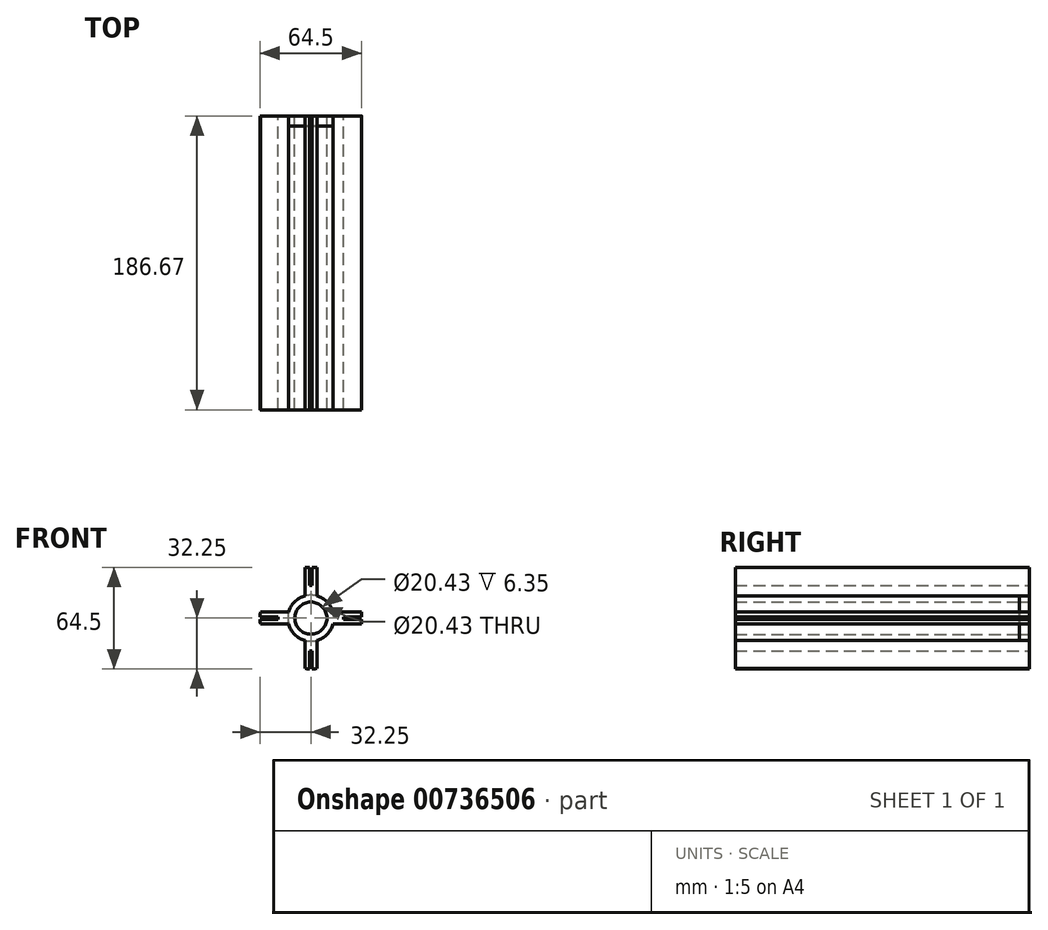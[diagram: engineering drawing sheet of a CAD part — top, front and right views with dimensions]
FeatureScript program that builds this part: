
annotation { "Feature Type Name" : "Feature", "Feature Type Description" : "" }
export const myFeature = defineFeature(function(context is Context, id is Id, definition is map)
    precondition{}
    {
        {
            var Q0;
            Q0=qCreatedBy(makeId("Front.planeOp"),FACE);
            var sketch = newSketch(context, id + "F0", { "sketchPlane" : qUnion([Q0])});
            skCircle(sketch, "E0", {"center": v(0, 0) * mm, "radius": 32.26 * mm});
            skCircle(sketch, "E1", {"center": v(-18.27, 15.72) * mm, "radius": 1.59 * mm});
            skCircle(sketch, "E2.MirrorC", {"center": v(18.27, 15.72) * mm, "radius": 1.59 * mm});
            skCircle(sketch, "E3.MirrorC", {"center": v(18.27, -15.72) * mm, "radius": 1.59 * mm});
            skCircle(sketch, "E4.MirrorC", {"center": v(-18.27, -15.72) * mm, "radius": 1.59 * mm});
            skCircle(sketch, "E5", {"center": v(0, 0) * mm, "radius": 14.6 * mm});
            skLineSegment(sketch, "E6", {"start": v(-20.83, 0) * mm, "end": v(-20.83, 0.83) * mm});
            skLineSegment(sketch, "E7", {"start": v(-20.83, 0.83) * mm, "end": v(-32.25, 0.83) * mm});
            skLineSegment(sketch, "E8.MirrorCS", {"start": v(-20.83, -0.83) * mm, "end": v(-32.25, -0.83) * mm});
            skLineSegment(sketch, "E9.MirrorCS", {"start": v(-20.83, 0) * mm, "end": v(-20.83, -0.83) * mm});
            skLineSegment(sketch, "E10.MirrorCS", {"start": v(20.83, 0.83) * mm, "end": v(32.25, 0.83) * mm});
            skLineSegment(sketch, "E11.MirrorCS", {"start": v(20.83, 0) * mm, "end": v(20.83, 0.83) * mm});
            skLineSegment(sketch, "E12.MirrorCS", {"start": v(20.83, -0.83) * mm, "end": v(32.25, -0.83) * mm});
            skLineSegment(sketch, "E13.MirrorCS", {"start": v(20.83, 0) * mm, "end": v(20.83, -0.83) * mm});
            skLineSegment(sketch, "E14", {"start": v(0, -20.83) * mm, "end": v(0.83, -20.83) * mm});
            skLineSegment(sketch, "E15", {"start": v(0.83, -20.83) * mm, "end": v(0.83, -32.25) * mm});
            skLineSegment(sketch, "E16.MirrorCS", {"start": v(0, -20.83) * mm, "end": v(-0.83, -20.83) * mm});
            skLineSegment(sketch, "E17.MirrorCS", {"start": v(-0.83, -20.83) * mm, "end": v(-0.83, -32.25) * mm});
            skLineSegment(sketch, "E18.MirrorCS", {"start": v(0.83, 20.83) * mm, "end": v(0.83, 32.25) * mm});
            skLineSegment(sketch, "E19.MirrorCS", {"start": v(-0.83, 20.83) * mm, "end": v(-0.83, 32.25) * mm});
            skLineSegment(sketch, "E20.MirrorCS", {"start": v(0, 20.83) * mm, "end": v(-0.83, 20.83) * mm});
            skLineSegment(sketch, "E21.MirrorCS", {"start": v(0, 20.83) * mm, "end": v(0.83, 20.83) * mm});
            skCircle(sketch, "E22", {"center": v(0, 0) * mm, "radius": 10.21 * mm});
            skLineSegment(sketch, "E23", {"start": v(0.83, 20.83) * mm, "end": v(3.83, 20.83) * mm});
            skLineSegment(sketch, "E24", {"start": v(3.83, 20.83) * mm, "end": v(3.83, 32.03) * mm});
            skLineSegment(sketch, "E25.MirrorCS", {"start": v(-3.83, 20.83) * mm, "end": v(-3.83, 32.03) * mm});
            skLineSegment(sketch, "E26.MirrorCS", {"start": v(-0.83, 20.83) * mm, "end": v(-3.83, 20.83) * mm});
            skLineSegment(sketch, "E27.MirrorCS", {"start": v(3.83, -20.83) * mm, "end": v(3.83, -32.03) * mm});
            skLineSegment(sketch, "E28.MirrorCS", {"start": v(-3.83, -20.83) * mm, "end": v(-3.83, -32.03) * mm});
            skLineSegment(sketch, "E29.MirrorCS", {"start": v(-0.83, -20.83) * mm, "end": v(-3.83, -20.83) * mm});
            skLineSegment(sketch, "E30.MirrorCS", {"start": v(0.83, -20.83) * mm, "end": v(3.83, -20.83) * mm});
            skLineSegment(sketch, "E31", {"start": v(20.83, 0.83) * mm, "end": v(20.83, 3.83) * mm});
            skLineSegment(sketch, "E32", {"start": v(20.83, 3.83) * mm, "end": v(32.03, 3.83) * mm});
            skLineSegment(sketch, "E33.MirrorCS", {"start": v(20.83, -3.83) * mm, "end": v(32.03, -3.83) * mm});
            skLineSegment(sketch, "E34.MirrorCS", {"start": v(20.83, -0.83) * mm, "end": v(20.83, -3.83) * mm});
            skLineSegment(sketch, "E35.MirrorCS", {"start": v(-20.83, 3.83) * mm, "end": v(-32.03, 3.83) * mm});
            skLineSegment(sketch, "E36.MirrorCS", {"start": v(-20.83, 0.83) * mm, "end": v(-20.83, 3.83) * mm});
            skLineSegment(sketch, "E37.MirrorCS", {"start": v(-20.83, -0.83) * mm, "end": v(-20.83, -3.83) * mm});
            skLineSegment(sketch, "E38.MirrorCS", {"start": v(-20.83, -3.83) * mm, "end": v(-32.03, -3.83) * mm});
            skLineSegment(sketch, "E39", {"start": v(20.83, 3.83) * mm, "end": v(14.09, 3.83) * mm});
            skLineSegment(sketch, "E40", {"start": v(20.83, -3.83) * mm, "end": v(14.09, -3.83) * mm});
            skLineSegment(sketch, "E41.MirrorCS", {"start": v(-20.83, -3.83) * mm, "end": v(-14.09, -3.83) * mm});
            skLineSegment(sketch, "E42.MirrorCS", {"start": v(-20.83, 3.83) * mm, "end": v(-14.09, 3.83) * mm});
            skLineSegment(sketch, "E43", {"start": v(-3.83, -20.83) * mm, "end": v(-3.83, -14.09) * mm});
            skLineSegment(sketch, "E44.MirrorCS", {"start": v(-3.83, 20.83) * mm, "end": v(-3.83, 14.09) * mm});
            skLineSegment(sketch, "E45.MirrorCS", {"start": v(3.83, -20.83) * mm, "end": v(3.83, -14.09) * mm});
            skLineSegment(sketch, "E46.MirrorCS", {"start": v(3.83, 20.83) * mm, "end": v(3.83, 14.09) * mm});
            skSolve(sketch);
        }
        {
            var Q0;
            Q0=makeQuery(id+"F0.imprint","IMPRINT",FACE,{"disambiguationData":[TD([[makeQuery(id+"F0.imprint","IMPRINT",EDGE,{"derivedFrom":sQuery(id+"F0.wireOp",EDGE,"E6")}),-1.0]])]});
            var Q1;
            {var subQ0=sQuery(id+"F0.wireOp",EDGE,"E7");Q1=makeQuery(id+"F0.imprint","IMPRINT",FACE,{"disambiguationData":[TD([[makeQuery(id+"F0.imprint","IMPRINT",EDGE,{"derivedFrom":subQ0}),-1.0]])]});}
            var Q2;
            {var subQ0=sQuery(id+"F0.wireOp",EDGE,"E8.MirrorCS");Q2=makeQuery(id+"F0.imprint","IMPRINT",FACE,{"disambiguationData":[TD([[makeQuery(id+"F0.imprint","IMPRINT",EDGE,{"derivedFrom":subQ0}),1.0]])]});}
            var Q3;
            Q3=makeQuery(id+"F0.imprint","IMPRINT",FACE,{"disambiguationData":[TD([[makeQuery(id+"F0.imprint","IMPRINT",EDGE,{"derivedFrom":sQuery(id+"F0.wireOp",EDGE,"E22")}),-1.0]])]});
            var Q4;
            Q4=makeQuery(id+"F0.imprint","IMPRINT",FACE,{"disambiguationData":[TD([[makeQuery(id+"F0.imprint","IMPRINT",EDGE,{"derivedFrom":sQuery(id+"F0.wireOp",EDGE,"E14")}),1.0]])]});
            var Q5;
            {var subQ0=sQuery(id+"F0.wireOp",EDGE,"E17.MirrorCS");Q5=makeQuery(id+"F0.imprint","IMPRINT",FACE,{"disambiguationData":[TD([[makeQuery(id+"F0.imprint","IMPRINT",EDGE,{"derivedFrom":subQ0}),-1.0]])]});}
            var Q6;
            {var subQ0=sQuery(id+"F0.wireOp",EDGE,"E15");Q6=makeQuery(id+"F0.imprint","IMPRINT",FACE,{"disambiguationData":[TD([[makeQuery(id+"F0.imprint","IMPRINT",EDGE,{"derivedFrom":subQ0}),1.0]])]});}
            var Q7;
            Q7=makeQuery(id+"F0.imprint","IMPRINT",FACE,{"disambiguationData":[TD([[makeQuery(id+"F0.imprint","IMPRINT",EDGE,{"derivedFrom":sQuery(id+"F0.wireOp",EDGE,"E11.MirrorCS")}),1.0]])]});
            var Q8;
            {var subQ0=sQuery(id+"F0.wireOp",EDGE,"E10.MirrorCS");Q8=makeQuery(id+"F0.imprint","IMPRINT",FACE,{"disambiguationData":[TD([[makeQuery(id+"F0.imprint","IMPRINT",EDGE,{"derivedFrom":subQ0}),1.0]])]});}
            var Q9;
            {var subQ0=sQuery(id+"F0.wireOp",EDGE,"E12.MirrorCS");Q9=makeQuery(id+"F0.imprint","IMPRINT",FACE,{"disambiguationData":[TD([[makeQuery(id+"F0.imprint","IMPRINT",EDGE,{"derivedFrom":subQ0}),-1.0]])]});}
            var Q10;
            Q10=makeQuery(id+"F0.imprint","IMPRINT",FACE,{"disambiguationData":[TD([[makeQuery(id+"F0.imprint","IMPRINT",EDGE,{"derivedFrom":sQuery(id+"F0.wireOp",EDGE,"E20.MirrorCS")}),1.0]])]});
            var Q11;
            {var subQ0=sQuery(id+"F0.wireOp",EDGE,"E19.MirrorCS");Q11=makeQuery(id+"F0.imprint","IMPRINT",FACE,{"disambiguationData":[TD([[makeQuery(id+"F0.imprint","IMPRINT",EDGE,{"derivedFrom":subQ0}),1.0]])]});}
            var Q12;
            {var subQ0=sQuery(id+"F0.wireOp",EDGE,"E18.MirrorCS");Q12=makeQuery(id+"F0.imprint","IMPRINT",FACE,{"disambiguationData":[TD([[makeQuery(id+"F0.imprint","IMPRINT",EDGE,{"derivedFrom":subQ0}),-1.0]])]});}
            extrude(context, id + "F1", {"entities" : qUnion([Q0, Q1, Q2, Q3, Q4, Q5, Q6, Q7, Q8, Q9, Q10, Q11, Q12]), "depth" : 186.67 * mm, "offsetDistance" : 25.4 * mm});
        }
        {
            var Q0;
            Q0=makeQuery(id+"F0.imprint","IMPRINT",FACE,{"disambiguationData":[TD([[makeQuery(id+"F0.imprint","IMPRINT",EDGE,{"derivedFrom":sQuery(id+"F0.wireOp",EDGE,"E5")}),1.0]])]});
            extrude(context, id + "F2", {"entities" : qUnion([Q0]), "depth" : 6.35 * mm, "offsetDistance" : 25.4 * mm});
        }
    });
